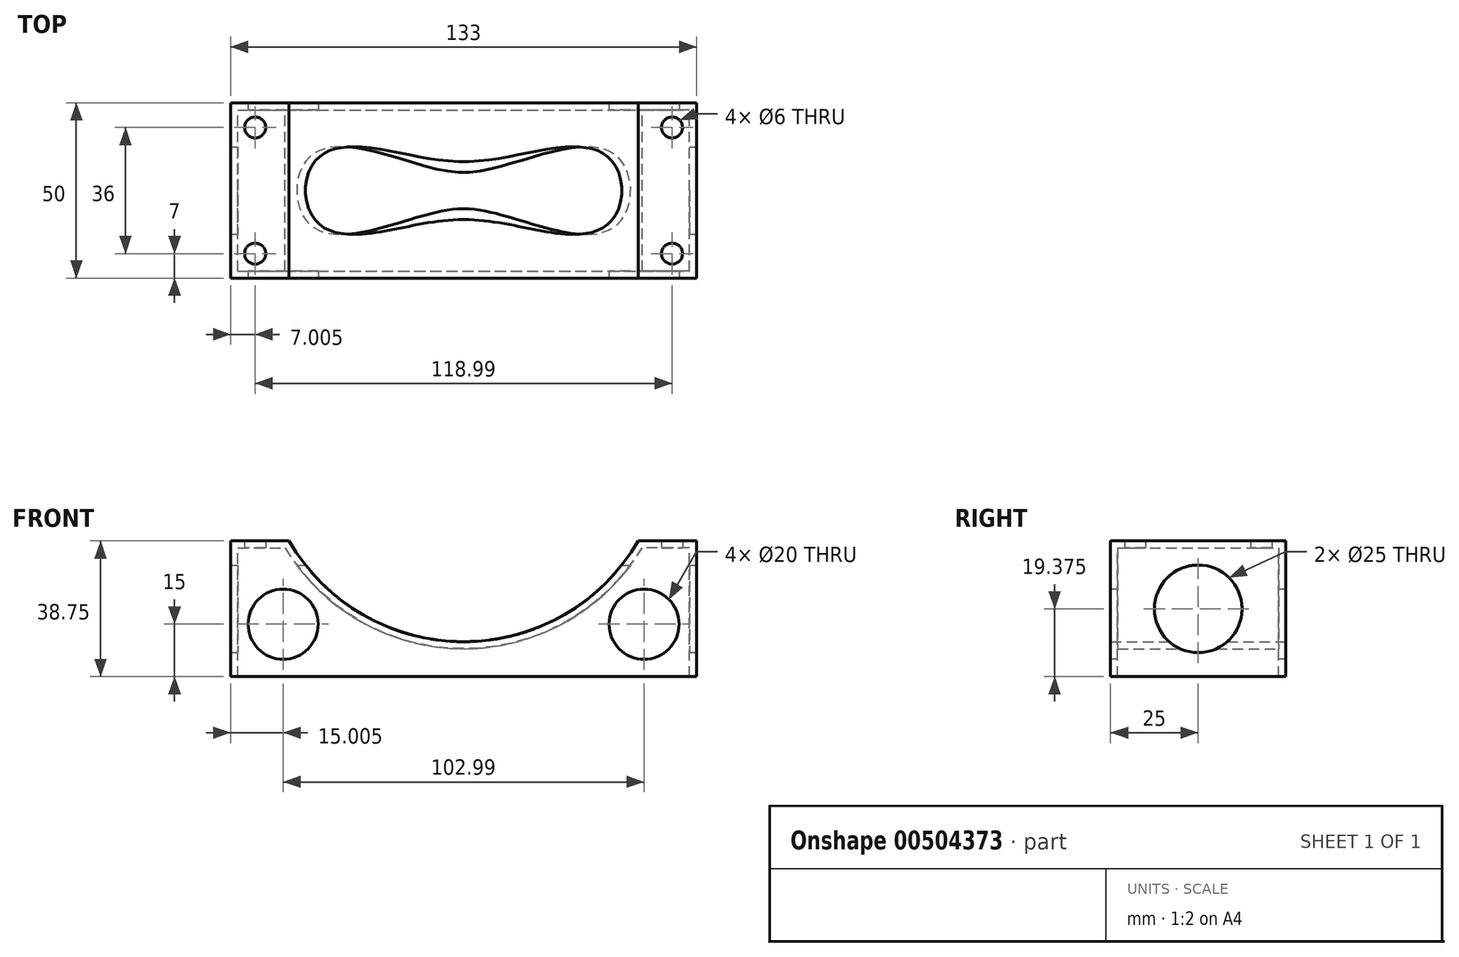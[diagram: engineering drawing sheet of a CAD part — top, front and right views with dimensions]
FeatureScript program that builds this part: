
annotation { "Feature Type Name" : "Feature", "Feature Type Description" : "" }
export const myFeature = defineFeature(function(context is Context, id is Id, definition is map)
    precondition{}
    {
        {
            var Q0;
            Q0=qCreatedBy(makeId("Front.planeOp"),FACE);
            var sketch = newSketch(context, id + "F0", { "sketchPlane" : qUnion([Q0])});
            skArc(sketch, "E0", {"start": v(-49.8, -28.75) * mm, "mid": v(0, -57.5) * mm, "end": v(49.8, -28.75) * mm});
            skPoint(sketch, "E1", {"position": v(-66.5, 0) * mm});
            skPoint(sketch, "E2", {"position": v(60, 0) * mm});
            skPoint(sketch, "E3", {"position": v(0, -60) * mm});
            skLineSegment(sketch, "E4.top", {"start": v(0, -67.5) * mm, "end": v(-43.3, -67.5) * mm});
            skLineSegment(sketch, "E5.MirrorCS", {"start": v(0, -67.5) * mm, "end": v(43.3, -67.5) * mm});
            skLineSegment(sketch, "E6", {"start": v(-66.5, -28.75) * mm, "end": v(-61.04, -28.75) * mm});
            skPoint(sketch, "E7.orphan", {"position": v(66.5, 0) * mm});
            skPoint(sketch, "E8", {"position": v(-49.8, -28.75) * mm});
            skPoint(sketch, "E9", {"position": v(49.8, -28.75) * mm});
            skPoint(sketch, "E4.right.start.orphan", {"position": v(-71.19, -52.5) * mm});
            skPoint(sketch, "E10.MirrorCS.end.orphan", {"position": v(71.19, -52.5) * mm});
            skPoint(sketch, "E11.orphan", {"position": v(66.5, -67.5) * mm});
            skPoint(sketch, "E12.orphan", {"position": v(-66.5, -67.5) * mm});
            skLineSegment(sketch, "E13.bottom", {"start": v(-66.5, -67.5) * mm, "end": v(-49.8, -67.5) * mm});
            skLineSegment(sketch, "E13.top", {"start": v(-66.5, -28.75) * mm, "end": v(-49.8, -28.75) * mm});
            skLineSegment(sketch, "E13.left", {"start": v(-66.5, -67.5) * mm, "end": v(-66.5, -28.75) * mm});
            skLineSegment(sketch, "E14.bottom", {"start": v(66.5, -67.5) * mm, "end": v(43.3, -67.5) * mm});
            skLineSegment(sketch, "E14.top", {"start": v(66.5, -28.75) * mm, "end": v(49.8, -28.75) * mm});
            skLineSegment(sketch, "E14.left", {"start": v(66.5, -67.5) * mm, "end": v(66.5, -28.75) * mm});
            skCircle(sketch, "E15", {"center": v(-51.5, -52.5) * mm, "radius": 10 * mm, "construction": true});
            skCircle(sketch, "E16.MirrorC", {"center": v(51.5, -52.5) * mm, "radius": 10 * mm, "construction": true});
            skLineSegment(sketch, "E17", {"start": v(-49.8, -67.5) * mm, "end": v(-43.3, -67.5) * mm});
            skSolve(sketch);
        }
        {
            var Q0;
            Q0 = qSketchRegion(id + "F0", true);
            extrude(context, id + "F1", {"entities" : qUnion([Q0]), "depth" : 25 * mm, "offsetDistance" : 25 * mm, "hasSecondDirection" : true, "secondDirectionOppositeDirection" : true, "secondDirectionDepth" : 25 * mm});
        }
        {
            var Q0;
            Q0=makeQuery(id+"F1.opExtrude","SWEPT_FACE",FACE,{"disambiguationData":[OSD([sQuery(id+"F0.wireOp",EDGE,"E4.top"),sQuery(id+"F0.wireOp",EDGE,"E5.MirrorCS")])]});
            shell(context, id + "F2", {"entities" : qUnion([Q0]), "thickness" : 2 * mm});
        }
        {
            var Q0;
            Q0=makeQuery(id+"F1.opExtrude","SWEPT_FACE",FACE,{"disambiguationData":[OSD([sQuery(id+"F0.wireOp",EDGE,"E4.top"),sQuery(id+"F0.wireOp",EDGE,"E5.MirrorCS"),sQuery(id+"F0.wireOp",EDGE,"E13.bottom"),sQuery(id+"F0.wireOp",EDGE,"E14.bottom")])]});
            var sketch = newSketch(context, id + "F3", { "sketchPlane" : qUnion([Q0])});
            skCircle(sketch, "E18", {"center": v(59.5, 18) * mm, "radius": 3 * mm});
            skCircle(sketch, "E19.MirrorC", {"center": v(-59.5, 18) * mm, "radius": 3 * mm});
            skCircle(sketch, "E20.MirrorC", {"center": v(59.5, -18) * mm, "radius": 3 * mm});
            skCircle(sketch, "E21.MirrorC", {"center": v(-59.5, -18) * mm, "radius": 3 * mm});
            skSolve(sketch);
        }
        {
            var Q0;
            Q0 = qSketchRegion(id + "F3", true);
            extrude(context, id + "F4", {"entities" : qUnion([Q0]), "operationType" : NewBodyOperationType.REMOVE, "oppositeDirection" : true, "depth" : 73 * mm, "offsetDistance" : 25 * mm});
        }
        {
            var Q0;
            Q0=makeQuery(id+"F1.opExtrude","SWEPT_FACE",FACE,{"disambiguationData":[OSD([sQuery(id+"F0.wireOp",EDGE,"E13.left")])]});
            var sketch = newSketch(context, id + "F5", { "sketchPlane" : qUnion([Q0])});
            skLineSegment(sketch, "E22.0.0", {"start": v(-25, -28.75) * mm, "end": v(-25, -67.5) * mm});
            skLineSegment(sketch, "E22.0.1", {"start": v(-25, -67.5) * mm, "end": v(25, -67.5) * mm});
            skLineSegment(sketch, "E22.0.2", {"start": v(25, -67.5) * mm, "end": v(25, -28.75) * mm});
            skLineSegment(sketch, "E22.0.3", {"start": v(25, -28.75) * mm, "end": v(-25, -28.75) * mm});
            skPoint(sketch, "E23", {"position": v(0, -48.12) * mm});
            skPoint(sketch, "E23.positionSnap0", {"position": v(-25, -48.12) * mm});
            skPoint(sketch, "E23.positionSnap1", {"position": v(0, -28.75) * mm});
            skCircle(sketch, "E24", {"center": v(0, -48.12) * mm, "radius": 12.5 * mm});
            skSolve(sketch);
        }
        {
            var Q0;
            Q0=makeQuery(id+"F1.opExtrude","SWEPT_FACE",FACE,{"disambiguationData":[OSD([sQuery(id+"F0.wireOp",EDGE,"E14.left")])]});
            var sketch = newSketch(context, id + "F6", { "sketchPlane" : qUnion([Q0])});
            skCircle(sketch, "E25.0", {"center": v(0, -48.12) * mm, "radius": 12.5 * mm});
            skSolve(sketch);
        }
        {
            var Q0;
            Q0 = qSketchRegion(id + "F6", true);
            extrude(context, id + "F7", {"entities" : qUnion([Q0]), "operationType" : NewBodyOperationType.REMOVE, "oppositeDirection" : true, "depth" : 142.6 * mm, "offsetDistance" : 25 * mm});
        }
        {
            var Q0;
            Q0=makeQuery(id+"F1.opExtrude","CAP_FACE",FACE,{"disambiguationData":[OSD([sQuery(id+"F0.wireOp",EDGE,"E0"),sQuery(id+"F0.wireOp",EDGE,"E4.top"),sQuery(id+"F0.wireOp",EDGE,"E5.MirrorCS"),sQuery(id+"F0.wireOp",EDGE,"E13.bottom"),sQuery(id+"F0.wireOp",EDGE,"E13.top"),sQuery(id+"F0.wireOp",EDGE,"E13.left"),sQuery(id+"F0.wireOp",EDGE,"E14.bottom"),sQuery(id+"F0.wireOp",EDGE,"E14.top"),sQuery(id+"F0.wireOp",EDGE,"E14.left")])],"isStart":true});
            var sketch = newSketch(context, id + "F8", { "sketchPlane" : qUnion([Q0])});
            skCircle(sketch, "E26.0", {"center": v(-51.5, -52.5) * mm, "radius": 10 * mm});
            skCircle(sketch, "E27.0", {"center": v(51.5, -52.5) * mm, "radius": 10 * mm});
            skSolve(sketch);
        }
        {
            var Q0;
            Q0 = qSketchRegion(id + "F8", true);
            extrude(context, id + "F9", {"entities" : qUnion([Q0]), "operationType" : NewBodyOperationType.REMOVE, "depth" : 5 * mm, "offsetDistance" : 25 * mm, "hasSecondDirection" : true, "secondDirectionOppositeDirection" : true, "secondDirectionDepth" : 60 * mm});
        }
    });
